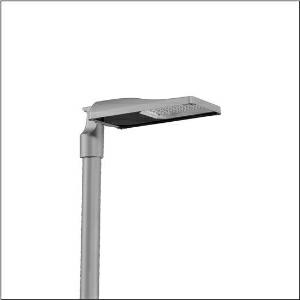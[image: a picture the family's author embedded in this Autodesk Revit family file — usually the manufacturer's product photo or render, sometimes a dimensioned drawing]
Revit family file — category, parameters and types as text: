
# Revit family: streetlight_sl_31_mini___p1_0a_5xh6a31a08ga_6892
name_source: partatom
category: Lighting Fixtures
units: mm (PartAtom-declared; Revit-internal decimal feet)

## family parameters
Cut with Voids When Loaded = No
Host = Face
Light Source = No
Part Type = Normal
Room Calculation Point = No
Round Connector Dimension = Use Diameter
Shared = No

## types (1)
- --- (1 x LED, 5550 lm, 37.3 W, 3000K)
    Apparent Load = 37 VA
    CIE Flux Codes = 23 55 94 100 100
    Color Rendering = 70
    Color Temperature = 3000K
    Default Elevation = 1800 mm
    Description = Streetlight SL 31 mini Easy, Desk-Remote mast luminaire for post-top, side-entry; light control with lens of PMMA; light distribution: P1.0a, direct asymmetric distribution, for standard-compliant lighting for roads and squares; LED: luminous flux: 5.550lm, light colour: 730, colour temperature: 3000K; luminous efficacy: 148,8lm/W; control: pre-setting: linear dimming characteristic, flexible luminous flux parameterisation, time-dependent luminous flux control, constant luminous flux control, intelligent temperature release in ECG and LED module, overheat protection; luminaire housing, of diecast aluminium, SITECO metallic grey (DB 702S), corrosivity category C5 high according to DIN EN ISO 12944; cover of toughened safety glass, transparent, opened without tools; mast flange of diecast aluminium, SITECO metallic grey (DB 702S), spigot size: 76/60mm, mast flange included unmounted; cable length: 6,5m, connection cable pre-assembled; mains connection: 220..240V, AC, 50/60Hz; power consumption (at start of service life): 37,3W / (at end of service life): 38,7W / (with reduced operation 50%): 17,5W; protection rating (complete): IP66; insulation class (complete): insulation class II (safety insulation); impact resistance: IK10; certification: CE, ENEC, ENEC+, VDE, UKCA; permissible operating ambient temperature for outdoor applications: -40..+50°C; packaging unit: 1 piece

Light Distribution: P1.0a
    Height = 76 mm
    Lamp = 1 x LED
    Lamp Light Flux = 5550 lm
    Lamp Power = 37.3 W
    Lamp count = 1
    Length = 547 mm
    Luminous efficacy = 149 lm/W
    Manufacturer = Siteco
    ModVariant = No
    Model = 5XH6A31A08GA
    Number of Poles = 1
    OnlyDefault = Yes
    Power Factor = 1
    Product Name = Streetlight SL 31 mini | P1.0a
    Product group = mast luminaire | pylon top
    ProductGroupID = 6100
    Protection Class = Protection class II
    Protection Degree = IP 66
    RLX_Detail_Level = 1
    RLX_Emergency_Light_Flux = 0 lm
    RLX_Emergency_Type = 0
    RLX_Emergency_Type_DB = No
    RlxData = <blob elided: 39313 chars, md5=f4ed001f>
    Socket = socket
    Standby Power = 0 W
    System Light Flux = 5550 lm
    System Power = 37 W
    Type Comments = factory setting: luminous flux: 100 % | dim-lin: 254 | 386 mA
    Type Image = l_1300326.jpg
    URL = http://relux.com
    VarID = @adj_064693
    Voltage = 0 V
    Weight = 0.00 kg
    Width = 265 mm

## geometry (parser evidence)
native form markers: Blend x4, Sweep x8
no freeform markers — native parametric forms only
